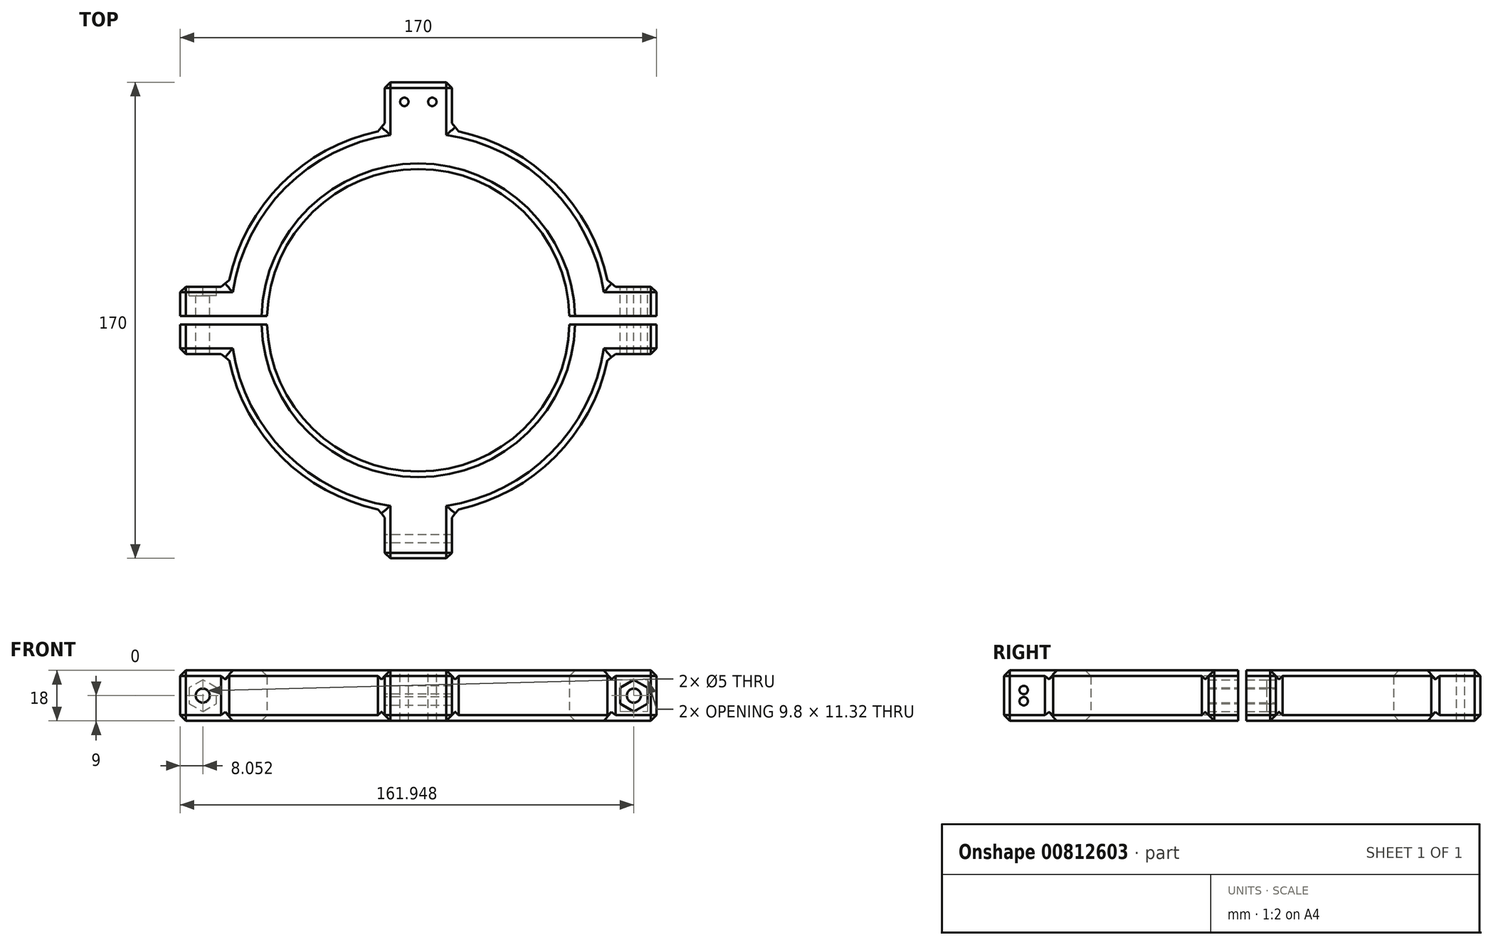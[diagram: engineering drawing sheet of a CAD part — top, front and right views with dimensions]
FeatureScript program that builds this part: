
annotation { "Feature Type Name" : "Feature", "Feature Type Description" : "" }
export const myFeature = defineFeature(function(context is Context, id is Id, definition is map)
    precondition{}
    {
        {
            var Q0;
            Q0=qCreatedBy(makeId("Top.planeOp"),FACE);
            var sketch = newSketch(context, id + "F0", { "sketchPlane" : qUnion([Q0])});
            skCircle(sketch, "E0", {"center": v(0, 0) * mm, "radius": 54 * mm});
            skCircle(sketch, "E1", {"center": v(0, 0) * mm, "radius": 69 * mm});
            skLineSegment(sketch, "E2.bottom", {"start": v(-85, 12) * mm, "end": v(-65, 12) * mm});
            skLineSegment(sketch, "E2.top", {"start": v(-85, -12) * mm, "end": v(-65, -12) * mm});
            skLineSegment(sketch, "E2.left", {"start": v(-85, 12) * mm, "end": v(-85, -12) * mm});
            skLineSegment(sketch, "E2.right", {"start": v(-65, 12) * mm, "end": v(-65, -12) * mm});
            skLineSegment(sketch, "E3.1.0", {"start": v(-12, -85) * mm, "end": v(12, -85) * mm});
            skLineSegment(sketch, "E3.1.1", {"start": v(-12, -85) * mm, "end": v(-12, -65) * mm});
            skLineSegment(sketch, "E3.1.2", {"start": v(12, -85) * mm, "end": v(12, -65) * mm});
            skLineSegment(sketch, "E3.1.3", {"start": v(-12, -65) * mm, "end": v(12, -65) * mm});
            skLineSegment(sketch, "E3.2.0", {"start": v(85, -12) * mm, "end": v(85, 12) * mm});
            skLineSegment(sketch, "E3.2.1", {"start": v(85, -12) * mm, "end": v(65, -12) * mm});
            skLineSegment(sketch, "E3.2.2", {"start": v(85, 12) * mm, "end": v(65, 12) * mm});
            skLineSegment(sketch, "E3.2.3", {"start": v(65, -12) * mm, "end": v(65, 12) * mm});
            skLineSegment(sketch, "E3.3.0", {"start": v(12, 85) * mm, "end": v(-12, 85) * mm});
            skLineSegment(sketch, "E3.3.1", {"start": v(12, 85) * mm, "end": v(12, 65) * mm});
            skLineSegment(sketch, "E3.3.2", {"start": v(-12, 85) * mm, "end": v(-12, 65) * mm});
            skLineSegment(sketch, "E3.3.3", {"start": v(12, 65) * mm, "end": v(-12, 65) * mm});
            skSolve(sketch);
        }
        {
            var Q0;
            Q0 = qSketchRegion(id + "F0", true);
            extrude(context, id + "F1", {"entities" : qUnion([Q0]), "depth" : 9 * mm, "offsetDistance" : 25 * mm, "hasSecondDirection" : true, "secondDirectionOppositeDirection" : true, "secondDirectionDepth" : 9 * mm});
        }
        {
            var Q0;
            Q0=makeQuery(id+"F1.opExtrude","SWEPT_FACE",FACE,{"disambiguationData":[OSD([sQuery(id+"F0.wireOp",EDGE,"E2.bottom")])]});
            var sketch = newSketch(context, id + "F2", { "sketchPlane" : qUnion([Q0])});
            skCircle(sketch, "E4", {"center": v(76.95, 0) * mm, "radius": 2.5 * mm});
            skCircle(sketch, "E5.MirrorC", {"center": v(-76.95, 0) * mm, "radius": 2.5 * mm});
            skCircle(sketch, "E6.cCircle", {"center": v(76.95, 0) * mm, "radius": 4.9 * mm, "construction": true});
            skLineSegment(sketch, "E6.0", {"start": v(72.05, -2.83) * mm, "end": v(72.05, 2.83) * mm});
            skLineSegment(sketch, "E6.1", {"start": v(72.05, 2.83) * mm, "end": v(76.95, 5.66) * mm});
            skLineSegment(sketch, "E6.2", {"start": v(76.95, 5.66) * mm, "end": v(81.85, 2.83) * mm});
            skLineSegment(sketch, "E6.3", {"start": v(81.85, 2.83) * mm, "end": v(81.85, -2.83) * mm});
            skLineSegment(sketch, "E6.4", {"start": v(81.85, -2.83) * mm, "end": v(76.95, -5.66) * mm});
            skLineSegment(sketch, "E6.5", {"start": v(76.95, -5.66) * mm, "end": v(72.05, -2.83) * mm});
            skPoint(sketch, "E6.0.midPoint", {"position": v(72.05, 0) * mm});
            skLineSegment(sketch, "E7.MirrorCS", {"start": v(-76.95, 5.66) * mm, "end": v(-81.85, 2.83) * mm});
            skLineSegment(sketch, "E8.MirrorCS", {"start": v(-81.85, 2.83) * mm, "end": v(-81.85, -2.83) * mm});
            skLineSegment(sketch, "E9.MirrorCS", {"start": v(-81.85, -2.83) * mm, "end": v(-76.95, -5.66) * mm});
            skLineSegment(sketch, "E10.MirrorCS", {"start": v(-76.95, -5.66) * mm, "end": v(-72.05, -2.83) * mm});
            skLineSegment(sketch, "E11.MirrorCS", {"start": v(-72.05, 2.83) * mm, "end": v(-76.95, 5.66) * mm});
            skLineSegment(sketch, "E12.MirrorCS", {"start": v(-72.05, -2.83) * mm, "end": v(-72.05, 2.83) * mm});
            skSolve(sketch);
        }
        {
            var Q0;
            Q0=makeQuery(id+"F2.imprint","IMPRINT",FACE,{"disambiguationData":[TD([[makeQuery(id+"F2.imprint","IMPRINT",EDGE,{"derivedFrom":sQuery(id+"F2.wireOp",EDGE,"E4")}),1.0]])]});
            var Q1;
            Q1=makeQuery(id+"F2.imprint","IMPRINT",FACE,{"disambiguationData":[TD([[makeQuery(id+"F2.imprint","IMPRINT",EDGE,{"derivedFrom":sQuery(id+"F2.wireOp",EDGE,"E5.MirrorC")}),-1.0]])]});
            var Q2;
            Q2=makeQuery(id+"F1.opExtrude","SWEPT_FACE",FACE,{"disambiguationData":[OSD([sQuery(id+"F0.wireOp",EDGE,"E2.top")])]});
            extrude(context, id + "F3", {"entities" : qUnion([Q0, Q1]), "operationType" : NewBodyOperationType.REMOVE, "endBound" : BoundingType.UP_TO_SURFACE, "oppositeDirection" : true, "depth" : 40 * mm, "endBoundEntityFace" : qUnion([Q2]), "offsetDistance" : 25 * mm});
        }
        {
            var Q0;
            Q0 = qSketchRegion(id + "F2", true);
            extrude(context, id + "F4", {"entities" : qUnion([Q0]), "operationType" : NewBodyOperationType.REMOVE, "oppositeDirection" : true, "depth" : 3.25 * mm, "offsetDistance" : 25 * mm});
        }
        {
            var Q0;
            Q0=makeQuery(id+"F1.opExtrude","CAP_FACE",FACE,{"disambiguationData":[OSD([sQuery(id+"F0.wireOp",EDGE,"E0"),sQuery(id+"F0.wireOp",EDGE,"E1"),sQuery(id+"F0.wireOp",EDGE,"E2.bottom"),sQuery(id+"F0.wireOp",EDGE,"E2.top"),sQuery(id+"F0.wireOp",EDGE,"E2.left"),sQuery(id+"F0.wireOp",EDGE,"E3.1.0"),sQuery(id+"F0.wireOp",EDGE,"E3.1.1"),sQuery(id+"F0.wireOp",EDGE,"E3.1.2"),sQuery(id+"F0.wireOp",EDGE,"E3.2.0"),sQuery(id+"F0.wireOp",EDGE,"E3.2.1"),sQuery(id+"F0.wireOp",EDGE,"E3.2.2"),sQuery(id+"F0.wireOp",EDGE,"E3.3.0"),sQuery(id+"F0.wireOp",EDGE,"E3.3.1"),sQuery(id+"F0.wireOp",EDGE,"E3.3.2")])],"isStart":false});
            var sketch = newSketch(context, id + "F5", { "sketchPlane" : qUnion([Q0])});
            skCircle(sketch, "E13", {"center": v(-5, 78) * mm, "radius": 1.5 * mm});
            skCircle(sketch, "E14.MirrorC", {"center": v(5, 78) * mm, "radius": 1.5 * mm});
            skSolve(sketch);
        }
        {
            var Q0;
            Q0 = qSketchRegion(id + "F5", true);
            var Q1;
            Q1=makeQuery(id+"F1.opExtrude","CAP_FACE",FACE,{"disambiguationData":[OSD([sQuery(id+"F0.wireOp",EDGE,"E0"),sQuery(id+"F0.wireOp",EDGE,"E1"),sQuery(id+"F0.wireOp",EDGE,"E2.bottom"),sQuery(id+"F0.wireOp",EDGE,"E2.top"),sQuery(id+"F0.wireOp",EDGE,"E2.left"),sQuery(id+"F0.wireOp",EDGE,"E3.1.0"),sQuery(id+"F0.wireOp",EDGE,"E3.1.1"),sQuery(id+"F0.wireOp",EDGE,"E3.1.2"),sQuery(id+"F0.wireOp",EDGE,"E3.2.0"),sQuery(id+"F0.wireOp",EDGE,"E3.2.1"),sQuery(id+"F0.wireOp",EDGE,"E3.2.2"),sQuery(id+"F0.wireOp",EDGE,"E3.3.0"),sQuery(id+"F0.wireOp",EDGE,"E3.3.1"),sQuery(id+"F0.wireOp",EDGE,"E3.3.2")])],"isStart":true});
            extrude(context, id + "F6", {"entities" : qUnion([Q0]), "operationType" : NewBodyOperationType.REMOVE, "endBound" : BoundingType.UP_TO_SURFACE, "oppositeDirection" : true, "depth" : 25 * mm, "endBoundEntityFace" : qUnion([Q1]), "offsetDistance" : 25 * mm});
        }
        {
            var Q0;
            Q0=makeQuery(id+"F1.opExtrude","SWEPT_FACE",FACE,{"disambiguationData":[OSD([sQuery(id+"F0.wireOp",EDGE,"E3.1.1")])]});
            var sketch = newSketch(context, id + "F7", { "sketchPlane" : qUnion([Q0])});
            skCircle(sketch, "E15", {"center": v(78, -2) * mm, "radius": 1.5 * mm});
            skCircle(sketch, "E16.MirrorC", {"center": v(78, 2) * mm, "radius": 1.5 * mm});
            skSolve(sketch);
        }
        {
            var Q0;
            Q0 = qSketchRegion(id + "F7", true);
            var Q1;
            Q1=makeQuery(id+"F1.opExtrude","SWEPT_FACE",FACE,{"disambiguationData":[OSD([sQuery(id+"F0.wireOp",EDGE,"E3.1.2")])]});
            extrude(context, id + "F8", {"entities" : qUnion([Q0]), "operationType" : NewBodyOperationType.REMOVE, "endBound" : BoundingType.UP_TO_SURFACE, "oppositeDirection" : true, "depth" : 25 * mm, "endBoundEntityFace" : qUnion([Q1]), "offsetDistance" : 25 * mm});
        }
        {
            var Q0;
            Q0=makeQuery(id+"F1.opExtrude","CAP_FACE",FACE,{"disambiguationData":[OSD([sQuery(id+"F0.wireOp",EDGE,"E0"),sQuery(id+"F0.wireOp",EDGE,"E1"),sQuery(id+"F0.wireOp",EDGE,"E2.bottom"),sQuery(id+"F0.wireOp",EDGE,"E2.top"),sQuery(id+"F0.wireOp",EDGE,"E2.left"),sQuery(id+"F0.wireOp",EDGE,"E3.1.0"),sQuery(id+"F0.wireOp",EDGE,"E3.1.1"),sQuery(id+"F0.wireOp",EDGE,"E3.1.2"),sQuery(id+"F0.wireOp",EDGE,"E3.2.0"),sQuery(id+"F0.wireOp",EDGE,"E3.2.1"),sQuery(id+"F0.wireOp",EDGE,"E3.2.2"),sQuery(id+"F0.wireOp",EDGE,"E3.3.0"),sQuery(id+"F0.wireOp",EDGE,"E3.3.1"),sQuery(id+"F0.wireOp",EDGE,"E3.3.2")])],"isStart":false});
            var sketch = newSketch(context, id + "F9", { "sketchPlane" : qUnion([Q0])});
            skLineSegment(sketch, "E17.bottom", {"start": v(-90, 1.5) * mm, "end": v(90, 1.5) * mm});
            skLineSegment(sketch, "E17.top", {"start": v(-90, -1.5) * mm, "end": v(90, -1.5) * mm});
            skLineSegment(sketch, "E17.left", {"start": v(-90, 1.5) * mm, "end": v(-90, -1.5) * mm});
            skLineSegment(sketch, "E17.right", {"start": v(90, 1.5) * mm, "end": v(90, -1.5) * mm});
            skSolve(sketch);
        }
        {
            var Q0;
            {var subQ0=sQuery(id+"F9.wireOp",EDGE,"E17.bottom");var subQ1=makeQuery(id+"F1.opExtrude","CAP_EDGE",EDGE,{"disambiguationData":[OSD([sQuery(id+"F0.wireOp",EDGE,"E2.left")])],"isStart":false});var subQ2=makeQuery(id+"F9.imprint","INTERSECT",VERTEX,{"derivedFrom":[subQ1,subQ0]});Q0=makeQuery(id+"F9.imprint","IMPRINT",FACE,{"disambiguationData":[TD([[makeQuery(id+"F9.imprint","IMPRINT",EDGE,{"disambiguationData":[TD([[subQ2,-1.0]])],"derivedFrom":subQ0}),-1.0]])]});}
            var Q1;
            {var subQ0=sQuery(id+"F9.wireOp",EDGE,"E17.bottom");var subQ1=makeQuery(id+"F1.opExtrude","CAP_EDGE",EDGE,{"disambiguationData":[OSD([sQuery(id+"F0.wireOp",EDGE,"E0")])],"isStart":false});var subQ2=makeQuery(id+"F9.imprint","INTERSECT",VERTEX,{"disambiguationData":[OD(0.0)],"derivedFrom":[subQ1,subQ0]});Q1=makeQuery(id+"F9.imprint","IMPRINT",FACE,{"disambiguationData":[TD([[makeQuery(id+"F9.imprint","IMPRINT",EDGE,{"disambiguationData":[TD([[subQ2,-1.0]])],"derivedFrom":subQ0}),-1.0]])]});}
            var Q2;
            {var subQ0=sQuery(id+"F9.wireOp",EDGE,"E17.bottom");var subQ1=makeQuery(id+"F1.opExtrude","CAP_EDGE",EDGE,{"disambiguationData":[OSD([sQuery(id+"F0.wireOp",EDGE,"E3.2.0")])],"isStart":false});var subQ2=makeQuery(id+"F9.imprint","INTERSECT",VERTEX,{"derivedFrom":[subQ1,subQ0]});Q2=makeQuery(id+"F9.imprint","IMPRINT",FACE,{"disambiguationData":[TD([[makeQuery(id+"F9.imprint","IMPRINT",EDGE,{"disambiguationData":[TD([[subQ2,1.0]])],"derivedFrom":subQ0}),-1.0]])]});}
            var Q3;
            {var subQ0=sQuery(id+"F9.wireOp",EDGE,"E17.right");Q3=makeQuery(id+"F9.imprint","IMPRINT",FACE,{"disambiguationData":[TD([[makeQuery(id+"F9.imprint","IMPRINT",EDGE,{"derivedFrom":subQ0}),-1.0]])]});}
            var Q4;
            {var subQ0=sQuery(id+"F9.wireOp",EDGE,"E17.left");Q4=makeQuery(id+"F9.imprint","IMPRINT",FACE,{"disambiguationData":[TD([[makeQuery(id+"F9.imprint","IMPRINT",EDGE,{"derivedFrom":subQ0}),1.0]])]});}
            var Q5;
            Q5=makeQuery(id+"F1.opExtrude","CAP_FACE",FACE,{"disambiguationData":[OSD([sQuery(id+"F0.wireOp",EDGE,"E0"),sQuery(id+"F0.wireOp",EDGE,"E1"),sQuery(id+"F0.wireOp",EDGE,"E2.bottom"),sQuery(id+"F0.wireOp",EDGE,"E2.top"),sQuery(id+"F0.wireOp",EDGE,"E2.left"),sQuery(id+"F0.wireOp",EDGE,"E3.1.0"),sQuery(id+"F0.wireOp",EDGE,"E3.1.1"),sQuery(id+"F0.wireOp",EDGE,"E3.1.2"),sQuery(id+"F0.wireOp",EDGE,"E3.2.0"),sQuery(id+"F0.wireOp",EDGE,"E3.2.1"),sQuery(id+"F0.wireOp",EDGE,"E3.2.2"),sQuery(id+"F0.wireOp",EDGE,"E3.3.0"),sQuery(id+"F0.wireOp",EDGE,"E3.3.1"),sQuery(id+"F0.wireOp",EDGE,"E3.3.2")])],"isStart":true});
            extrude(context, id + "F10", {"entities" : qUnion([Q0, Q1, Q2, Q3, Q4]), "operationType" : NewBodyOperationType.REMOVE, "endBound" : BoundingType.UP_TO_SURFACE, "oppositeDirection" : true, "depth" : 25 * mm, "endBoundEntityFace" : qUnion([Q5]), "offsetDistance" : 25 * mm});
        }
        {
            var Q0;
            {var subQ0=sQuery(id+"F0.wireOp",EDGE,"E1");Q0=makeQuery(id+"F1.opExtrude","CAP_EDGE",EDGE,{"disambiguationData":[OSD([subQ0]),TDD([makeQuery(id+"F0.imprint","IMPRINT",EDGE,{"disambiguationData":[TD([[makeQuery(id+"F0.imprint","INTERSECT",VERTEX,{"derivedFrom":[subQ0,sQuery(id+"F0.wireOp",EDGE,"E3.3.2")]}),-1.0]])],"derivedFrom":subQ0})])],"isStart":false});}
            var Q1;
            Q1=makeQuery(id+"F1.opExtrude","CAP_EDGE",EDGE,{"disambiguationData":[OSD([sQuery(id+"F0.wireOp",EDGE,"E2.bottom")])],"isStart":false});
            var Q2;
            {var subQ0=sQuery(id+"F0.wireOp",EDGE,"E2.left");var subQ1=sQuery(id+"F0.wireOp",EDGE,"E2.bottom");Q2=makeQuery(id+"F10.boolean.opBoolean","SPLIT",EDGE,{"disambiguationData":[TD([makeQuery(id+"F1.opExtrude","SWEPT_FACE",FACE,{"disambiguationData":[OSD([subQ1])]})])],"derivedFrom":makeQuery(id+"F1.opExtrude","CAP_EDGE",EDGE,{"disambiguationData":[OSD([subQ0])],"isStart":false})});}
            var Q3;
            {var subQ0=sQuery(id+"F0.wireOp",EDGE,"E0");Q3=makeQuery(id+"F10.boolean.opBoolean","SPLIT",EDGE,{"disambiguationData":[TD([makeQuery(id+"F10.opExtrude","SWEPT_FACE",FACE,{"disambiguationData":[OSD([sQuery(id+"F9.wireOp",EDGE,"E17.bottom")])]})])],"derivedFrom":makeQuery(id+"F1.opExtrude","CAP_EDGE",EDGE,{"disambiguationData":[OSD([subQ0])],"isStart":false})});}
            var Q4;
            Q4=makeQuery(id+"F1.opExtrude","CAP_EDGE",EDGE,{"disambiguationData":[OSD([sQuery(id+"F0.wireOp",EDGE,"E3.3.2")])],"isStart":false});
            var Q5;
            Q5=makeQuery(id+"F1.opExtrude","CAP_EDGE",EDGE,{"disambiguationData":[OSD([sQuery(id+"F0.wireOp",EDGE,"E3.3.0")])],"isStart":false});
            var Q6;
            Q6=makeQuery(id+"F1.opExtrude","CAP_EDGE",EDGE,{"disambiguationData":[OSD([sQuery(id+"F0.wireOp",EDGE,"E3.3.1")])],"isStart":false});
            var Q7;
            {var subQ0=sQuery(id+"F0.wireOp",EDGE,"E1");Q7=makeQuery(id+"F1.opExtrude","CAP_EDGE",EDGE,{"disambiguationData":[OSD([subQ0]),TDD([makeQuery(id+"F0.imprint","IMPRINT",EDGE,{"disambiguationData":[TD([[makeQuery(id+"F0.imprint","INTERSECT",VERTEX,{"derivedFrom":[subQ0,sQuery(id+"F0.wireOp",EDGE,"E3.3.1")]}),1.0]])],"derivedFrom":subQ0})])],"isStart":false});}
            var Q8;
            Q8=makeQuery(id+"F1.opExtrude","CAP_EDGE",EDGE,{"disambiguationData":[OSD([sQuery(id+"F0.wireOp",EDGE,"E3.2.2")])],"isStart":false});
            var Q9;
            {var subQ0=sQuery(id+"F0.wireOp",EDGE,"E3.2.2");var subQ1=sQuery(id+"F0.wireOp",EDGE,"E3.2.0");Q9=makeQuery(id+"F10.boolean.opBoolean","SPLIT",EDGE,{"disambiguationData":[TD([makeQuery(id+"F1.opExtrude","SWEPT_FACE",FACE,{"disambiguationData":[OSD([subQ0])]})])],"derivedFrom":makeQuery(id+"F1.opExtrude","CAP_EDGE",EDGE,{"disambiguationData":[OSD([subQ1])],"isStart":false})});}
            var Q10;
            {var subQ0=sQuery(id+"F0.wireOp",EDGE,"E2.left");var subQ1=sQuery(id+"F0.wireOp",EDGE,"E2.top");Q10=makeQuery(id+"F10.boolean.opBoolean","SPLIT",EDGE,{"disambiguationData":[TD([makeQuery(id+"F1.opExtrude","SWEPT_FACE",FACE,{"disambiguationData":[OSD([subQ1])]})])],"derivedFrom":makeQuery(id+"F1.opExtrude","CAP_EDGE",EDGE,{"disambiguationData":[OSD([subQ0])],"isStart":false})});}
            var Q11;
            {var subQ0=sQuery(id+"F0.wireOp",EDGE,"E1");Q11=makeQuery(id+"F1.opExtrude","CAP_EDGE",EDGE,{"disambiguationData":[OSD([subQ0]),TDD([makeQuery(id+"F0.imprint","IMPRINT",EDGE,{"disambiguationData":[TD([[makeQuery(id+"F0.imprint","INTERSECT",VERTEX,{"derivedFrom":[subQ0,sQuery(id+"F0.wireOp",EDGE,"E2.top")]}),-1.0]])],"derivedFrom":subQ0})])],"isStart":false});}
            var Q12;
            Q12=makeQuery(id+"F1.opExtrude","CAP_EDGE",EDGE,{"disambiguationData":[OSD([sQuery(id+"F0.wireOp",EDGE,"E2.top")])],"isStart":false});
            var Q13;
            {var subQ0=sQuery(id+"F0.wireOp",EDGE,"E0");Q13=makeQuery(id+"F10.boolean.opBoolean","SPLIT",EDGE,{"disambiguationData":[TD([makeQuery(id+"F10.opExtrude","SWEPT_FACE",FACE,{"disambiguationData":[OSD([sQuery(id+"F9.wireOp",EDGE,"E17.top")])]})])],"derivedFrom":makeQuery(id+"F1.opExtrude","CAP_EDGE",EDGE,{"disambiguationData":[OSD([subQ0])],"isStart":false})});}
            var Q14;
            Q14=makeQuery(id+"F1.opExtrude","CAP_EDGE",EDGE,{"disambiguationData":[OSD([sQuery(id+"F0.wireOp",EDGE,"E3.1.1")])],"isStart":false});
            var Q15;
            Q15=makeQuery(id+"F1.opExtrude","CAP_EDGE",EDGE,{"disambiguationData":[OSD([sQuery(id+"F0.wireOp",EDGE,"E3.1.0")])],"isStart":false});
            var Q16;
            Q16=makeQuery(id+"F1.opExtrude","CAP_EDGE",EDGE,{"disambiguationData":[OSD([sQuery(id+"F0.wireOp",EDGE,"E3.1.2")])],"isStart":false});
            var Q17;
            {var subQ0=sQuery(id+"F0.wireOp",EDGE,"E1");Q17=makeQuery(id+"F1.opExtrude","CAP_EDGE",EDGE,{"disambiguationData":[OSD([subQ0]),TDD([makeQuery(id+"F0.imprint","IMPRINT",EDGE,{"disambiguationData":[TD([[makeQuery(id+"F0.imprint","INTERSECT",VERTEX,{"derivedFrom":[subQ0,sQuery(id+"F0.wireOp",EDGE,"E3.1.2")]}),-1.0]])],"derivedFrom":subQ0})])],"isStart":false});}
            var Q18;
            Q18=makeQuery(id+"F1.opExtrude","CAP_EDGE",EDGE,{"disambiguationData":[OSD([sQuery(id+"F0.wireOp",EDGE,"E3.2.1")])],"isStart":false});
            var Q19;
            {var subQ0=sQuery(id+"F0.wireOp",EDGE,"E3.2.1");var subQ1=sQuery(id+"F0.wireOp",EDGE,"E3.2.0");Q19=makeQuery(id+"F10.boolean.opBoolean","SPLIT",EDGE,{"disambiguationData":[TD([makeQuery(id+"F1.opExtrude","SWEPT_FACE",FACE,{"disambiguationData":[OSD([subQ0])]})])],"derivedFrom":makeQuery(id+"F1.opExtrude","CAP_EDGE",EDGE,{"disambiguationData":[OSD([subQ1])],"isStart":false})});}
            var Q20;
            {var subQ0=sQuery(id+"F0.wireOp",EDGE,"E1");Q20=makeQuery(id+"F1.opExtrude","CAP_EDGE",EDGE,{"disambiguationData":[OSD([subQ0]),TDD([makeQuery(id+"F0.imprint","IMPRINT",EDGE,{"disambiguationData":[TD([[makeQuery(id+"F0.imprint","INTERSECT",VERTEX,{"derivedFrom":[subQ0,sQuery(id+"F0.wireOp",EDGE,"E3.3.2")]}),-1.0]])],"derivedFrom":subQ0})])],"isStart":true});}
            var Q21;
            Q21=makeQuery(id+"F1.opExtrude","CAP_EDGE",EDGE,{"disambiguationData":[OSD([sQuery(id+"F0.wireOp",EDGE,"E3.3.2")])],"isStart":true});
            var Q22;
            Q22=makeQuery(id+"F1.opExtrude","CAP_EDGE",EDGE,{"disambiguationData":[OSD([sQuery(id+"F0.wireOp",EDGE,"E3.3.0")])],"isStart":true});
            var Q23;
            Q23=makeQuery(id+"F1.opExtrude","CAP_EDGE",EDGE,{"disambiguationData":[OSD([sQuery(id+"F0.wireOp",EDGE,"E3.3.1")])],"isStart":true});
            var Q24;
            {var subQ0=sQuery(id+"F0.wireOp",EDGE,"E1");Q24=makeQuery(id+"F1.opExtrude","CAP_EDGE",EDGE,{"disambiguationData":[OSD([subQ0]),TDD([makeQuery(id+"F0.imprint","IMPRINT",EDGE,{"disambiguationData":[TD([[makeQuery(id+"F0.imprint","INTERSECT",VERTEX,{"derivedFrom":[subQ0,sQuery(id+"F0.wireOp",EDGE,"E3.3.1")]}),1.0]])],"derivedFrom":subQ0})])],"isStart":true});}
            var Q25;
            Q25=makeQuery(id+"F1.opExtrude","CAP_EDGE",EDGE,{"disambiguationData":[OSD([sQuery(id+"F0.wireOp",EDGE,"E3.2.2")])],"isStart":true});
            var Q26;
            {var subQ0=sQuery(id+"F0.wireOp",EDGE,"E3.2.2");var subQ1=sQuery(id+"F0.wireOp",EDGE,"E3.2.0");Q26=makeQuery(id+"F10.boolean.opBoolean","SPLIT",EDGE,{"disambiguationData":[TD([makeQuery(id+"F1.opExtrude","SWEPT_FACE",FACE,{"disambiguationData":[OSD([subQ0])]})])],"derivedFrom":makeQuery(id+"F1.opExtrude","CAP_EDGE",EDGE,{"disambiguationData":[OSD([subQ1])],"isStart":true})});}
            var Q27;
            {var subQ0=sQuery(id+"F0.wireOp",EDGE,"E3.2.1");var subQ1=sQuery(id+"F0.wireOp",EDGE,"E3.2.0");Q27=makeQuery(id+"F10.boolean.opBoolean","SPLIT",EDGE,{"disambiguationData":[TD([makeQuery(id+"F1.opExtrude","SWEPT_FACE",FACE,{"disambiguationData":[OSD([subQ0])]})])],"derivedFrom":makeQuery(id+"F1.opExtrude","CAP_EDGE",EDGE,{"disambiguationData":[OSD([subQ1])],"isStart":true})});}
            var Q28;
            Q28=makeQuery(id+"F1.opExtrude","CAP_EDGE",EDGE,{"disambiguationData":[OSD([sQuery(id+"F0.wireOp",EDGE,"E3.2.1")])],"isStart":true});
            var Q29;
            {var subQ0=sQuery(id+"F0.wireOp",EDGE,"E1");Q29=makeQuery(id+"F1.opExtrude","CAP_EDGE",EDGE,{"disambiguationData":[OSD([subQ0]),TDD([makeQuery(id+"F0.imprint","IMPRINT",EDGE,{"disambiguationData":[TD([[makeQuery(id+"F0.imprint","INTERSECT",VERTEX,{"derivedFrom":[subQ0,sQuery(id+"F0.wireOp",EDGE,"E3.1.2")]}),-1.0]])],"derivedFrom":subQ0})])],"isStart":true});}
            var Q30;
            Q30=makeQuery(id+"F1.opExtrude","CAP_EDGE",EDGE,{"disambiguationData":[OSD([sQuery(id+"F0.wireOp",EDGE,"E3.1.2")])],"isStart":true});
            var Q31;
            Q31=makeQuery(id+"F1.opExtrude","CAP_EDGE",EDGE,{"disambiguationData":[OSD([sQuery(id+"F0.wireOp",EDGE,"E3.1.0")])],"isStart":true});
            var Q32;
            Q32=makeQuery(id+"F1.opExtrude","CAP_EDGE",EDGE,{"disambiguationData":[OSD([sQuery(id+"F0.wireOp",EDGE,"E3.1.1")])],"isStart":true});
            var Q33;
            {var subQ0=sQuery(id+"F0.wireOp",EDGE,"E1");Q33=makeQuery(id+"F1.opExtrude","CAP_EDGE",EDGE,{"disambiguationData":[OSD([subQ0]),TDD([makeQuery(id+"F0.imprint","IMPRINT",EDGE,{"disambiguationData":[TD([[makeQuery(id+"F0.imprint","INTERSECT",VERTEX,{"derivedFrom":[subQ0,sQuery(id+"F0.wireOp",EDGE,"E2.top")]}),-1.0]])],"derivedFrom":subQ0})])],"isStart":true});}
            var Q34;
            Q34=makeQuery(id+"F1.opExtrude","CAP_EDGE",EDGE,{"disambiguationData":[OSD([sQuery(id+"F0.wireOp",EDGE,"E2.top")])],"isStart":true});
            var Q35;
            {var subQ0=sQuery(id+"F0.wireOp",EDGE,"E2.left");var subQ1=sQuery(id+"F0.wireOp",EDGE,"E2.top");Q35=makeQuery(id+"F10.boolean.opBoolean","SPLIT",EDGE,{"disambiguationData":[TD([makeQuery(id+"F1.opExtrude","SWEPT_FACE",FACE,{"disambiguationData":[OSD([subQ1])]})])],"derivedFrom":makeQuery(id+"F1.opExtrude","CAP_EDGE",EDGE,{"disambiguationData":[OSD([subQ0])],"isStart":true})});}
            var Q36;
            {var subQ0=sQuery(id+"F0.wireOp",EDGE,"E2.left");var subQ1=sQuery(id+"F0.wireOp",EDGE,"E2.bottom");Q36=makeQuery(id+"F10.boolean.opBoolean","SPLIT",EDGE,{"disambiguationData":[TD([makeQuery(id+"F1.opExtrude","SWEPT_FACE",FACE,{"disambiguationData":[OSD([subQ1])]})])],"derivedFrom":makeQuery(id+"F1.opExtrude","CAP_EDGE",EDGE,{"disambiguationData":[OSD([subQ0])],"isStart":true})});}
            var Q37;
            Q37=makeQuery(id+"F1.opExtrude","CAP_EDGE",EDGE,{"disambiguationData":[OSD([sQuery(id+"F0.wireOp",EDGE,"E2.bottom")])],"isStart":true});
            var Q38;
            Q38=makeQuery(id+"F1.opExtrude","SWEPT_EDGE",EDGE,{"disambiguationData":[OSD([sQuery(id+"F0.wireOp",EDGE,"E3.3.0"),sQuery(id+"F0.wireOp",EDGE,"E3.3.1")])]});
            var Q39;
            Q39=makeQuery(id+"F1.opExtrude","SWEPT_EDGE",EDGE,{"disambiguationData":[OSD([sQuery(id+"F0.wireOp",EDGE,"E3.3.0"),sQuery(id+"F0.wireOp",EDGE,"E3.3.2")])]});
            var Q40;
            Q40=makeQuery(id+"F1.opExtrude","SWEPT_EDGE",EDGE,{"disambiguationData":[OSD([sQuery(id+"F0.wireOp",EDGE,"E2.top"),sQuery(id+"F0.wireOp",EDGE,"E2.left")])]});
            var Q41;
            Q41=makeQuery(id+"F1.opExtrude","SWEPT_EDGE",EDGE,{"disambiguationData":[OSD([sQuery(id+"F0.wireOp",EDGE,"E2.bottom"),sQuery(id+"F0.wireOp",EDGE,"E2.left")])]});
            var Q42;
            {var subQ0=sQuery(id+"F0.wireOp",EDGE,"E0");Q42=makeQuery(id+"F10.boolean.opBoolean","SPLIT",EDGE,{"disambiguationData":[TD([makeQuery(id+"F10.opExtrude","SWEPT_FACE",FACE,{"disambiguationData":[OSD([sQuery(id+"F9.wireOp",EDGE,"E17.top")])]})])],"derivedFrom":makeQuery(id+"F1.opExtrude","CAP_EDGE",EDGE,{"disambiguationData":[OSD([subQ0])],"isStart":true})});}
            var Q43;
            {var subQ0=sQuery(id+"F0.wireOp",EDGE,"E0");Q43=makeQuery(id+"F10.boolean.opBoolean","SPLIT",EDGE,{"disambiguationData":[TD([makeQuery(id+"F10.opExtrude","SWEPT_FACE",FACE,{"disambiguationData":[OSD([sQuery(id+"F9.wireOp",EDGE,"E17.bottom")])]})])],"derivedFrom":makeQuery(id+"F1.opExtrude","CAP_EDGE",EDGE,{"disambiguationData":[OSD([subQ0])],"isStart":true})});}
            var Q44;
            Q44=makeQuery(id+"F1.opExtrude","SWEPT_EDGE",EDGE,{"disambiguationData":[OSD([sQuery(id+"F0.wireOp",EDGE,"E3.1.0"),sQuery(id+"F0.wireOp",EDGE,"E3.1.1")])]});
            var Q45;
            Q45=makeQuery(id+"F1.opExtrude","SWEPT_EDGE",EDGE,{"disambiguationData":[OSD([sQuery(id+"F0.wireOp",EDGE,"E3.1.0"),sQuery(id+"F0.wireOp",EDGE,"E3.1.2")])]});
            var Q46;
            Q46=makeQuery(id+"F1.opExtrude","SWEPT_EDGE",EDGE,{"disambiguationData":[OSD([sQuery(id+"F0.wireOp",EDGE,"E3.2.0"),sQuery(id+"F0.wireOp",EDGE,"E3.2.1")])]});
            var Q47;
            Q47=makeQuery(id+"F1.opExtrude","SWEPT_EDGE",EDGE,{"disambiguationData":[OSD([sQuery(id+"F0.wireOp",EDGE,"E3.2.0"),sQuery(id+"F0.wireOp",EDGE,"E3.2.2")])]});
            chamfer(context, id + "F11", {"entities" : qUnion([Q0, Q1, Q2, Q3, Q4, Q5, Q6, Q7, Q8, Q9, Q10, Q11, Q12, Q13, Q14, Q15, Q16, Q17, Q18, Q19, Q20, Q21, Q22, Q23, Q24, Q25, Q26, Q27, Q28, Q29, Q30, Q31, Q32, Q33, Q34, Q35, Q36, Q37, Q38, Q39, Q40, Q41, Q42, Q43, Q44, Q45, Q46, Q47]), "width" : 2 * mm, "tangentPropagation" : true});
        }
        {
            var Q0;
            Q0=makeQuery(id+"F1.opExtrude","SWEPT_EDGE",EDGE,{"disambiguationData":[OSD([sQuery(id+"F0.wireOp",EDGE,"E1"),sQuery(id+"F0.wireOp",EDGE,"E3.2.1")])]});
            var Q1;
            Q1=makeQuery(id+"F1.opExtrude","SWEPT_EDGE",EDGE,{"disambiguationData":[OSD([sQuery(id+"F0.wireOp",EDGE,"E1"),sQuery(id+"F0.wireOp",EDGE,"E3.1.2")])]});
            var Q2;
            Q2=makeQuery(id+"F1.opExtrude","SWEPT_EDGE",EDGE,{"disambiguationData":[OSD([sQuery(id+"F0.wireOp",EDGE,"E1"),sQuery(id+"F0.wireOp",EDGE,"E3.2.2")])]});
            var Q3;
            Q3=makeQuery(id+"F1.opExtrude","SWEPT_EDGE",EDGE,{"disambiguationData":[OSD([sQuery(id+"F0.wireOp",EDGE,"E1"),sQuery(id+"F0.wireOp",EDGE,"E3.1.1")])]});
            var Q4;
            Q4=makeQuery(id+"F1.opExtrude","SWEPT_EDGE",EDGE,{"disambiguationData":[OSD([sQuery(id+"F0.wireOp",EDGE,"E1"),sQuery(id+"F0.wireOp",EDGE,"E2.bottom")])]});
            var Q5;
            Q5=makeQuery(id+"F1.opExtrude","SWEPT_EDGE",EDGE,{"disambiguationData":[OSD([sQuery(id+"F0.wireOp",EDGE,"E1"),sQuery(id+"F0.wireOp",EDGE,"E2.top")])]});
            var Q6;
            Q6=makeQuery(id+"F1.opExtrude","SWEPT_EDGE",EDGE,{"disambiguationData":[OSD([sQuery(id+"F0.wireOp",EDGE,"E1"),sQuery(id+"F0.wireOp",EDGE,"E3.3.2")])]});
            var Q7;
            Q7=makeQuery(id+"F1.opExtrude","SWEPT_EDGE",EDGE,{"disambiguationData":[OSD([sQuery(id+"F0.wireOp",EDGE,"E1"),sQuery(id+"F0.wireOp",EDGE,"E3.3.1")])]});
            chamfer(context, id + "F12", {"entities" : qUnion([Q0, Q1, Q2, Q3, Q4, Q5, Q6, Q7]), "width" : 3 * mm, "tangentPropagation" : true});
        }
    });
